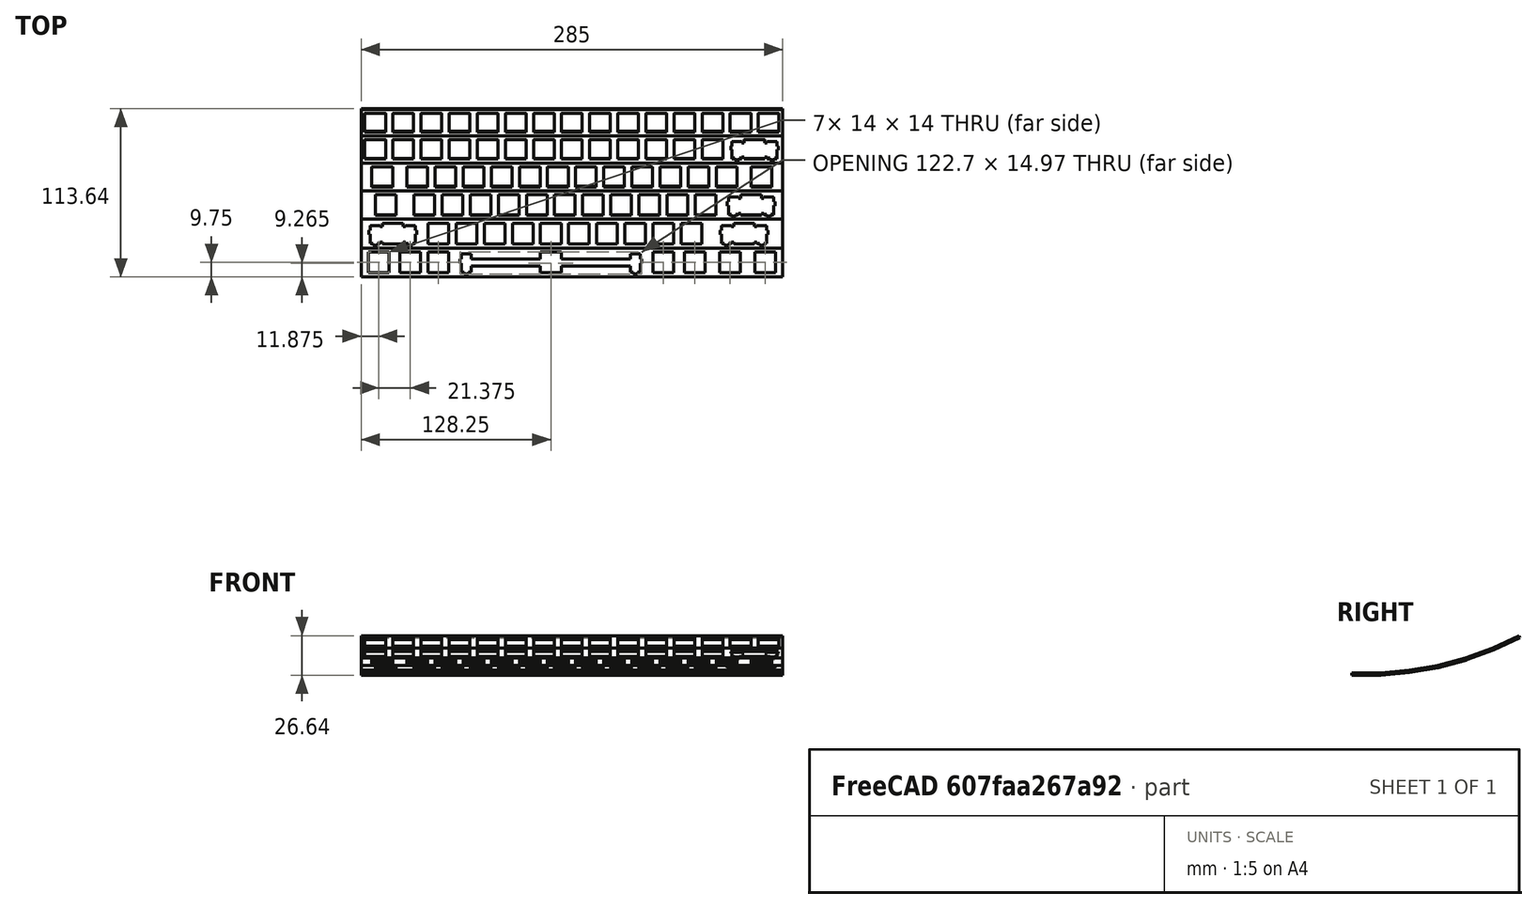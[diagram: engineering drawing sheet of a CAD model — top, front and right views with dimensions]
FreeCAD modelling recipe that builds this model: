
FCSTD DOCUMENT  (FreeCAD 1.0R38641 +468 (Git))
Label: case
License: GPL 3
objects: Sketcher::SketchObject×16, PartDesign::Pocket×15, PartDesign::LinearPattern×13, App::Part×2, Spreadsheet::Sheet×1, PartDesign::Pad×1, PartDesign::Body×1, App::FeaturePython×1, Assembly::JointGroup×1, Assembly::AssemblyObject×1
note: 107 computed .brp shape members not serialized (recipe doc carries the construction recipe); baked Part::Feature solids carry a one-line shape summary decoded from their .brp

FEATURE [Spreadsheet::Sheet] Spreadsheet  label="params"
  cells = A1='Parameter Name; B1='Value; C1='Note; A2='plate_thickness; B2(plate_thickness)==1.6 mm; A3='spacing_x; B3(spacing_x)==19 mm; A4='spacing_y; B4(spacing_y)==19.5 mm; A5='switch_width; B5(switch_width)==14 mm; A6='row_angle; B6(row_angle)==5 deg; A7='row_count; B7(row_count)=6; A8='column_count; B8(column_count)=15; A9='ctrlKey_width; B9(ctrlKey_width)=1.25; A10='enterKey_width; B10(enterKey_width)=2.25; A11='shiftKey_width; B11(shiftKey_width)=2.75; C11='Right Shift; A12='capsKey_width; B12(capsKey_width)=1.75; A13='tabKey_width; B13(tabKey_width)=1.5; A14='spaceBar_width; B14(spaceBar_width)=7; A15='backspace_width; B15(backspace_width)=2
FEATURE [Sketcher::SketchObject] Sketch  label="Profile"
  ArcFitTolerance = 1e-06
  FullyConstrained = true
  MakeInternals = false
  Placement = pos=(0,0,0) rot=(0.57735,0.57735,0.57735;2.0944rad)
  expr: Constraints[10] = <<params>>.spacing_y
  expr: Constraints[20] = <<params>>.row_angle
  expr: Constraints[52] = <<params>>.row_angle
  expr: Constraints[61] = <<params>>.row_angle
  expr: Constraints[62] = <<params>>.row_angle
  expr: Constraints[63] = <<params>>.row_angle
  expr: Constraints[9] = <<params>>.plate_thickness
  sketch-geometry (29):
    g0: LineSegment StartX=0 StartY=0 StartZ=0 EndX=19.5 EndY=0 EndZ=0
    g1: LineSegment [constr] StartX=19.5 StartY=0 StartZ=0 EndX=19.5 EndY=1.6 EndZ=0
    g2: LineSegment StartX=19.5 StartY=1.6 StartZ=0 EndX=0 EndY=1.6 EndZ=0
    g3: LineSegment StartX=0 StartY=1.6 StartZ=0 EndX=0 EndY=0 EndZ=0
    g4: LineSegment [constr] StartX=19.5 StartY=1.6 StartZ=0 EndX=19.6394 EndY=0.00608848 EndZ=0
    g5: LineSegment StartX=19.6394 StartY=0.00608848 StartZ=0 EndX=39.0652 EndY=1.70563 EndZ=0
    g6: LineSegment [constr] StartX=39.0652 StartY=1.70563 StartZ=0 EndX=38.9258 EndY=3.29954 EndZ=0
    g7: LineSegment StartX=38.9258 StartY=3.29954 StartZ=0 EndX=19.5 EndY=1.6 EndZ=0
    g8: LineSegment [constr] StartX=38.9258 StartY=3.29954 StartZ=0 EndX=39.2036 EndY=1.72384 EndZ=0
    g9: LineSegment StartX=39.2036 StartY=1.72384 StartZ=0 EndX=58.4074 EndY=5.10998 EndZ=0
    g10: LineSegment [constr] StartX=58.4074 StartY=5.10998 StartZ=0 EndX=58.1295 EndY=6.68568 EndZ=0
    g11: LineSegment StartX=58.1295 StartY=6.68568 StartZ=0 EndX=38.9258 EndY=3.29954 EndZ=0
    g12: LineSegment [constr] StartX=58.1295 StartY=6.68568 StartZ=0 EndX=58.5437 EndY=5.1402 EndZ=0
    g13: LineSegment StartX=58.5437 StartY=5.1402 StartZ=0 EndX=77.3792 EndY=10.1872 EndZ=0
    g14: LineSegment [constr] StartX=77.3792 StartY=10.1872 StartZ=0 EndX=76.9651 EndY=11.7326 EndZ=0
    g15: LineSegment StartX=76.9651 StartY=11.7326 StartZ=0 EndX=58.1295 EndY=6.68568 EndZ=0
    g16: LineSegment [constr] StartX=76.9651 StartY=11.7326 StartZ=0 EndX=77.5123 EndY=10.2291 EndZ=0
    g17: LineSegment StartX=77.5123 StartY=10.2291 StartZ=0 EndX=95.8363 EndY=16.8985 EndZ=0
    g18: LineSegment [constr] StartX=95.8363 StartY=16.8985 StartZ=0 EndX=95.2891 EndY=18.402 EndZ=0
    g19: LineSegment StartX=95.2891 StartY=18.402 StartZ=0 EndX=76.9651 EndY=11.7326 EndZ=0
    g20: LineSegment [constr] StartX=95.2891 StartY=18.402 StartZ=0 EndX=95.9653 EndY=16.9519 EndZ=0
    g21: LineSegment StartX=95.9653 StartY=16.9519 StartZ=0 EndX=113.638 EndY=25.193 EndZ=0
    g22: LineSegment StartX=113.638 StartY=25.193 StartZ=0 EndX=112.962 EndY=26.6431 EndZ=0
    g23: LineSegment StartX=112.962 StartY=26.6431 StartZ=0 EndX=95.2891 EndY=18.402 EndZ=0
    g24: ArcOfCircle CenterX=19.5 CenterY=1.6 CenterZ=0 NormalX=0 NormalY=0 NormalZ=1 AngleXU=0 Radius=1.6 StartAngle=4.71239 EndAngle=4.79966
    g25: ArcOfCircle CenterX=38.9258 CenterY=3.29954 CenterZ=0 NormalX=0 NormalY=0 NormalZ=1 AngleXU=0 Radius=1.6 StartAngle=4.79966 EndAngle=4.88692
    g26: ArcOfCircle CenterX=58.1295 CenterY=6.68568 CenterZ=0 NormalX=0 NormalY=0 NormalZ=1 AngleXU=0 Radius=1.6 StartAngle=4.88692 EndAngle=4.97419
    g27: ArcOfCircle CenterX=76.9651 CenterY=11.7326 CenterZ=0 NormalX=0 NormalY=0 NormalZ=1 AngleXU=0 Radius=1.6 StartAngle=4.97419 EndAngle=5.06145
    g28: ArcOfCircle CenterX=95.2891 CenterY=18.402 CenterZ=0 NormalX=0 NormalY=0 NormalZ=1 AngleXU=0 Radius=1.6 StartAngle=5.06145 EndAngle=5.14872
  constraints (76):
    c: Coincident(g0,g1)
    c: Coincident(g1,g2)
    c: Coincident(g2,g3)
    c: Coincident(g3,g0)
    c: Horizontal(g0)
    c: Horizontal(g2)
    c: Vertical(g1)
    c: Vertical(g3)
    c: Coincident(g0,g-1)
    c: DistanceY(g3,g3) = 1.6
    c: DistanceX(g2,g2) = 19.5
    c: Coincident(g4,g5)
    c: Coincident(g5,g6)
    c: Coincident(g6,g7)
    c: Coincident(g7,g4)
    c: Perpendicular(g7,g4)
    c: Perpendicular(g6,g7)
    c: Perpendicular(g5,g4)
    c: Equal(g7,g2)
    c: Coincident(g4,g1)
    c: Angle(g2,g7) = 0.0872665
    c: Coincident(g8,g9)
    c: Coincident(g9,g10)
    c: Coincident(g11,g8)
    c: Perpendicular(g11,g8)
    c: Perpendicular(g10,g11)
    c: Perpendicular(g9,g8)
    c: Coincident(g12,g13)
    c: Coincident(g13,g14)
    c: Coincident(g14,g15)
    c: Perpendicular(g15,g12)
    c: Perpendicular(g14,g15)
    c: Perpendicular(g13,g12)
    c: Coincident(g16,g17)
    c: Coincident(g17,g18)
    c: Coincident(g18,g19)
    c: Coincident(g19,g16)
    c: Perpendicular(g19,g16)
    c: Perpendicular(g18,g19)
    c: Perpendicular(g17,g16)
    c: Coincident(g20,g21)
    c: Coincident(g21,g22)
    c: Coincident(g22,g23)
    c: Coincident(g23,g20)
    c: Perpendicular(g23,g20)
    c: Perpendicular(g22,g23)
    c: Perpendicular(g21,g20)
    c: Equal(g11,g15)
    c: Equal(g15,g19)
    c: Equal(g19,g23)
    c: Equal(g23,g7)
    c: Coincident(g6,g8)
    c: Angle(g11,g15) = 0.0872665
    c: Coincident(g14,g16)
    c: Coincident(g20,g18)
    c: Coincident(g26,g9)
    c: Coincident(g26,g12)
    c: Coincident(g28,g18)
    c: Coincident(g28,g17)
    c: Coincident(g28,g20)
    c: Coincident(g25,g8)
    c: Angle(g7,g11) = 0.0872665
    c: Angle(g15,g19) = 0.0872665
    c: Angle(g19,g23) = 0.0872665
    c: Coincident(g25,g6)
    c: Coincident(g24,g0)
    c: Coincident(g24,g1)
    c: Coincident(g24,g4)
    c: Coincident(g25,g5)
    c: Coincident(g27,g13)
    c: Coincident(g27,g16)
    c: Coincident(g27,g14)
    c: Coincident(g26,g15)
    c: Coincident(g26,g12)
    c: Coincident(g26,g10)
    c: Coincident(g26,g11)
FEATURE [PartDesign::Pad] Pad
  Direction = (1,1e-16,-1e-16)
  Length = 285
  Length2 = 10
  Placement = pos=(0,0,0) rot=(0.57735,0.57735,0.57735;2.0944rad)
  Profile = -> Sketch
  ReferenceAxis = -> Sketch [N_Axis]
  Refine = true
  Suppressed = false
  Type = 0
  expr: Length = <<params>>.column_count * <<params>>.spacing_x
FEATURE [Sketcher::SketchObject] Sketch001
  ArcFitTolerance = 1e-06
  AttachmentSupport = -> [Pad]
  FullyConstrained = true
  MakeInternals = false
  MapMode = 5
  Placement = pos=(4e-16,-7e-16,1.6) rot=(0,0,-1;1.5708rad)
  expr: Constraints[11] = <<params>>.spacing_y / 2
  expr: Constraints[12] = (<<params>>.ctrlKey_width + 0.5) * <<params>>.spacing_x
  expr: Constraints[9] = <<params>>.switch_width
  sketch-geometry (5):
    g0: LineSegment StartX=-16.75 StartY=26.25 StartZ=0 EndX=-2.75 EndY=26.25 EndZ=0
    g1: LineSegment StartX=-2.75 StartY=26.25 StartZ=0 EndX=-2.75 EndY=40.25 EndZ=0
    g2: LineSegment StartX=-2.75 StartY=40.25 StartZ=0 EndX=-16.75 EndY=40.25 EndZ=0
    g3: LineSegment StartX=-16.75 StartY=40.25 StartZ=0 EndX=-16.75 EndY=26.25 EndZ=0
    g4: GeomPoint [constr] X=-9.75 Y=33.25 Z=0
  constraints (13):
    c: Coincident(g0,g1)
    c: Coincident(g1,g2)
    c: Coincident(g2,g3)
    c: Coincident(g3,g0)
    c: Horizontal(g0)
    c: Horizontal(g2)
    c: Vertical(g1)
    c: Vertical(g3)
    c: Symmetric(g2,g0,g4)
    c: DistanceX(g0,g0) = 14
    c: Equal(g0,g3)
    c: Distance(g4,g-2) = 9.75
    c: Distance(g4,g-1) = 33.25
FEATURE [Sketcher::SketchObject] Sketch002
  ArcFitTolerance = 1e-06
  AttachmentSupport = -> [Pad]
  ExternalGeometry = -> [Pad]
  FullyConstrained = true
  MakeInternals = false
  MapMode = 5
  Placement = pos=(0,0.00920587,-0.105224) rot=(0.043578,0.043578,-0.998099;1.5727rad)
  expr: Constraints[11] = (<<params>>.enterKey_width + 0.5) * <<params>>.spacing_x
  expr: Constraints[12] = <<params>>.spacing_y / 2
  expr: Constraints[9] = <<params>>.switch_width
  sketch-geometry (5):
    g0: LineSegment StartX=-36.3152 StartY=45.25 StartZ=0 EndX=-22.3152 EndY=45.25 EndZ=0
    g1: LineSegment StartX=-22.3152 StartY=45.25 StartZ=0 EndX=-22.3152 EndY=59.25 EndZ=0
    g2: LineSegment StartX=-22.3152 StartY=59.25 StartZ=0 EndX=-36.3152 EndY=59.25 EndZ=0
    g3: LineSegment StartX=-36.3152 StartY=59.25 StartZ=0 EndX=-36.3152 EndY=45.25 EndZ=0
    g4: GeomPoint [constr] X=-29.3152 Y=52.25 Z=0
  constraints (13):
    c: Coincident(g0,g1)
    c: Coincident(g1,g2)
    c: Coincident(g2,g3)
    c: Coincident(g3,g0)
    c: Horizontal(g0)
    c: Horizontal(g2)
    c: Vertical(g1)
    c: Vertical(g3)
    c: Symmetric(g2,g0,g4)
    c: DistanceX(g0,g0) = 14
    c: Equal(g0,g3)
    c: Distance(g4,g-1) = 52.25
    c: Distance(g4,g-3) = 9.75
FEATURE [Sketcher::SketchObject] Sketch003
  ArcFitTolerance = 1e-06
  AttachmentSupport = -> [Pad]
  ExternalGeometry = -> [Pad]
  FullyConstrained = true
  MakeInternals = false
  MapMode = 5
  Placement = pos=(-1.1e-15,0.609502,-3.45666) rot=(0.086827,0.086827,-0.992433;1.57839rad)
  expr: Constraints[11] = (<<params>>.capsKey_width + 0.5) * <<params>>.spacing_x
  expr: Constraints[12] = <<params>>.spacing_y / 2
  expr: Constraints[9] = <<params>>.switch_width
  sketch-geometry (5):
    g0: LineSegment StartX=-55.6574 StartY=35.75 StartZ=0 EndX=-41.6574 EndY=35.75 EndZ=0
    g1: LineSegment StartX=-41.6574 StartY=35.75 StartZ=0 EndX=-41.6574 EndY=49.75 EndZ=0
    g2: LineSegment StartX=-41.6574 StartY=49.75 StartZ=0 EndX=-55.6574 EndY=49.75 EndZ=0
    g3: LineSegment StartX=-55.6574 StartY=49.75 StartZ=0 EndX=-55.6574 EndY=35.75 EndZ=0
    g4: GeomPoint [constr] X=-48.6574 Y=42.75 Z=0
  constraints (13):
    c: Coincident(g0,g1)
    c: Coincident(g1,g2)
    c: Coincident(g2,g3)
    c: Coincident(g3,g0)
    c: Horizontal(g0)
    c: Horizontal(g2)
    c: Vertical(g1)
    c: Vertical(g3)
    c: Symmetric(g2,g0,g4)
    c: DistanceX(g0,g0) = 14
    c: Equal(g0,g3)
    c: Distance(g4,g-1) = 42.75
    c: Distance(g4,g-3) = 9.75
FEATURE [Sketcher::SketchObject] Sketch004
  ArcFitTolerance = 1e-06
  AttachmentSupport = -> [Pad]
  ExternalGeometry = -> [Pad]
  FullyConstrained = true
  MakeInternals = false
  MapMode = 5
  Placement = pos=(-3.1e-15,2.22252,-8.29457) rot=(0.129428,0.129428,-0.983106;1.58783rad)
  expr: Constraints[11] = (<<params>>.tabKey_width + 0.5) * <<params>>.spacing_x
  expr: Constraints[12] = <<params>>.spacing_y / 2
  expr: Constraints[9] = <<params>>.switch_width
  sketch-geometry (5):
    g0: LineSegment StartX=-74.6292 StartY=31 StartZ=0 EndX=-60.6292 EndY=31 EndZ=0
    g1: LineSegment StartX=-60.6292 StartY=31 StartZ=0 EndX=-60.6292 EndY=45 EndZ=0
    g2: LineSegment StartX=-60.6292 StartY=45 StartZ=0 EndX=-74.6292 EndY=45 EndZ=0
    g3: LineSegment StartX=-74.6292 StartY=45 StartZ=0 EndX=-74.6292 EndY=31 EndZ=0
    g4: GeomPoint [constr] X=-67.6292 Y=38 Z=0
  constraints (13):
    c: Coincident(g0,g1)
    c: Coincident(g1,g2)
    c: Coincident(g2,g3)
    c: Coincident(g3,g0)
    c: Horizontal(g0)
    c: Horizontal(g2)
    c: Vertical(g1)
    c: Vertical(g3)
    c: Symmetric(g2,g0,g4)
    c: DistanceX(g0,g0) = 14
    c: Equal(g0,g3)
    c: Distance(g4,g-1) = 38
    c: Distance(g4,g-3) = 9.75
FEATURE [Sketcher::SketchObject] Sketch005
  ArcFitTolerance = 1e-06
  AttachmentSupport = -> [Pad]
  ExternalGeometry = -> [Pad]
  FullyConstrained = true
  MakeInternals = false
  MapMode = 5
  Placement = pos=(-6.1e-15,5.23241,-14.3759) rot=(0.171088,0.171088,-0.970288;1.60095rad)
  expr: Constraints[11] = 0.5 * <<params>>.spacing_x
  expr: Constraints[12] = <<params>>.spacing_y / 2
  expr: Constraints[9] = <<params>>.switch_width
  sketch-geometry (5):
    g0: LineSegment StartX=-93.0863 StartY=2.5 StartZ=0 EndX=-79.0863 EndY=2.5 EndZ=0
    g1: LineSegment StartX=-79.0863 StartY=2.5 StartZ=0 EndX=-79.0863 EndY=16.5 EndZ=0
    g2: LineSegment StartX=-79.0863 StartY=16.5 StartZ=0 EndX=-93.0863 EndY=16.5 EndZ=0
    g3: LineSegment StartX=-93.0863 StartY=16.5 StartZ=0 EndX=-93.0863 EndY=2.5 EndZ=0
    g4: GeomPoint [constr] X=-86.0863 Y=9.5 Z=0
  constraints (13):
    c: Coincident(g0,g1)
    c: Coincident(g1,g2)
    c: Coincident(g2,g3)
    c: Coincident(g3,g0)
    c: Horizontal(g0)
    c: Horizontal(g2)
    c: Vertical(g1)
    c: Vertical(g3)
    c: Symmetric(g2,g0,g4)
    c: DistanceX(g0,g0) = 14
    c: Equal(g0,g3)
    c: Distance(g4,g-1) = 9.5
    c: Distance(g4,g-3) = 9.75
FEATURE [Sketcher::SketchObject] Sketch006
  ArcFitTolerance = 1e-06
  AttachmentSupport = -> [Pad]
  ExternalGeometry = -> [Pad]
  FullyConstrained = true
  MakeInternals = false
  MapMode = 5
  Placement = pos=(-1.03e-14,9.97083,-21.3825) rot=(0.211541,0.211541,-0.954201;1.61766rad)
  expr: Constraints[11] = 0.5 * <<params>>.spacing_x
  expr: Constraints[12] = <<params>>.spacing_y / 2
  expr: Constraints[9] = <<params>>.switch_width
  sketch-geometry (5):
    g0: LineSegment StartX=-110.888 StartY=2.5 StartZ=0 EndX=-96.8883 EndY=2.5 EndZ=0
    g1: LineSegment StartX=-96.8883 StartY=2.5 StartZ=0 EndX=-96.8883 EndY=16.5 EndZ=0
    g2: LineSegment StartX=-96.8883 StartY=16.5 StartZ=0 EndX=-110.888 EndY=16.5 EndZ=0
    g3: LineSegment StartX=-110.888 StartY=16.5 StartZ=0 EndX=-110.888 EndY=2.5 EndZ=0
    g4: GeomPoint [constr] X=-103.888 Y=9.5 Z=0
  constraints (13):
    c: Coincident(g0,g1)
    c: Coincident(g1,g2)
    c: Coincident(g2,g3)
    c: Coincident(g3,g0)
    c: Horizontal(g0)
    c: Horizontal(g2)
    c: Vertical(g1)
    c: Vertical(g3)
    c: Symmetric(g2,g0,g4)
    c: DistanceX(g0,g0) = 14
    c: Equal(g0,g3)
    c: Distance(g4,g-1) = 9.5
    c: Distance(g4,g-3) = 9.75
FEATURE [PartDesign::Pocket] Pocket
  BaseFeature = -> Pad
  Direction = (0,0,-1)
  Length = 5
  Length2 = 5
  Placement = pos=(0,0,0) rot=(0.57735,0.57735,0.57735;2.0944rad)
  Profile = -> Sketch001
  ReferenceAxis = -> Sketch001 [N_Axis]
  Refine = true
  Suppressed = false
  Type = 2
FEATURE [PartDesign::Pocket] Pocket001
  BaseFeature = -> Pocket
  Direction = (0,0.0871557,-0.996195)
  Length = 5
  Length2 = 5
  Placement = pos=(0,0,0) rot=(0.57735,0.57735,0.57735;2.0944rad)
  Profile = -> Sketch002
  ReferenceAxis = -> Sketch002 [N_Axis]
  Refine = true
  Suppressed = false
  Type = 2
FEATURE [PartDesign::Pocket] Pocket002
  BaseFeature = -> Pocket001
  Direction = (0,0.173648,-0.984808)
  Length = 5
  Length2 = 5
  Placement = pos=(0,0,0) rot=(0.57735,0.57735,0.57735;2.0944rad)
  Profile = -> Sketch003
  ReferenceAxis = -> Sketch003 [N_Axis]
  Refine = true
  Suppressed = false
  Type = 2
FEATURE [PartDesign::Pocket] Pocket003
  BaseFeature = -> Pocket002
  Direction = (0,0.258819,-0.965926)
  Length = 5
  Length2 = 5
  Placement = pos=(0,0,0) rot=(0.57735,0.57735,0.57735;2.0944rad)
  Profile = -> Sketch004
  ReferenceAxis = -> Sketch004 [N_Axis]
  Refine = true
  Suppressed = false
  Type = 2
FEATURE [PartDesign::Pocket] Pocket004
  BaseFeature = -> Pocket003
  Direction = (-1e-16,0.34202,-0.939693)
  Length = 5
  Length2 = 5
  Placement = pos=(0,0,0) rot=(0.57735,0.57735,0.57735;2.0944rad)
  Profile = -> Sketch005
  ReferenceAxis = -> Sketch005 [N_Axis]
  Refine = true
  Suppressed = false
  Type = 2
FEATURE [PartDesign::Pocket] Pocket005
  BaseFeature = -> Pocket004
  Direction = (-1e-16,0.422618,-0.906308)
  Length = 5
  Length2 = 5
  Placement = pos=(0,0,0) rot=(0.57735,0.57735,0.57735;2.0944rad)
  Profile = -> Sketch006
  ReferenceAxis = -> Sketch006 [N_Axis]
  Refine = true
  Suppressed = false
  Type = 2
FEATURE [PartDesign::LinearPattern] LinearPattern
  BaseFeature = -> Pocket005
  Direction = -> X_Axis002
  Length = 266
  Mode = 1
  Occurrences = 15
  Offset = 19
  Originals = -> [Pocket005]
  Placement = pos=(0,0,0) rot=(0.57735,0.57735,0.57735;2.0944rad)
  Refine = true
  Suppressed = false
  TransformMode = 0
  expr: Occurrences = <<params>>.column_count
  expr: Offset = <<params>>.spacing_x
FEATURE [PartDesign::LinearPattern] LinearPattern001
  BaseFeature = -> LinearPattern
  Direction = -> X_Axis002
  Length = 228
  Mode = 1
  Occurrences = 13
  Offset = 19
  Originals = -> [Pocket004]
  Placement = pos=(0,0,0) rot=(0.57735,0.57735,0.57735;2.0944rad)
  Refine = true
  Suppressed = false
  TransformMode = 0
  expr: Occurrences = <<params>>.column_count - <<params>>.backspace_width
  expr: Offset = <<params>>.spacing_x
FEATURE [PartDesign::LinearPattern] LinearPattern002
  BaseFeature = -> LinearPattern001
  Direction = -> X_Axis002
  Length = 19
  Mode = 1
  Occurrences = 2
  Offset = 19
  Originals = -> [Pocket]
  Placement = pos=(0,0,0) rot=(0.57735,0.57735,0.57735;2.0944rad)
  Refine = true
  Suppressed = false
  TransformMode = 0
  expr: Offset = <<params>>.spacing_x
FEATURE [PartDesign::LinearPattern] LinearPattern003
  BaseFeature = -> LinearPattern002
  Direction = -> X_Axis002
  Length = 171
  Mode = 1
  Occurrences = 10
  Offset = 19
  Originals = -> [Pocket001]
  Placement = pos=(0,0,0) rot=(0.57735,0.57735,0.57735;2.0944rad)
  Refine = true
  Suppressed = false
  TransformMode = 0
  expr: Occurrences = <<params>>.column_count - <<params>>.enterKey_width - <<params>>.shiftKey_width
  expr: Offset = <<params>>.spacing_x
FEATURE [PartDesign::LinearPattern] LinearPattern004
  BaseFeature = -> LinearPattern003
  Direction = -> X_Axis002
  Length = 190
  Mode = 1
  Occurrences = 11
  Offset = 19
  Originals = -> [Pocket002]
  Placement = pos=(0,0,0) rot=(0.57735,0.57735,0.57735;2.0944rad)
  Refine = true
  Suppressed = false
  TransformMode = 0
  expr: Occurrences = <<params>>.column_count - <<params>>.capsKey_width - <<params>>.enterKey_width
  expr: Offset = <<params>>.spacing_x
FEATURE [PartDesign::LinearPattern] LinearPattern005
  BaseFeature = -> LinearPattern004
  Direction = -> X_Axis002
  Length = 209
  Mode = 1
  Occurrences = 12
  Offset = 19
  Originals = -> [Pocket003]
  Placement = pos=(0,0,0) rot=(0.57735,0.57735,0.57735;2.0944rad)
  Refine = true
  Suppressed = false
  TransformMode = 0
  expr: Occurrences = <<params>>.column_count - 2 * <<params>>.tabKey_width
  expr: Offset = <<params>>.spacing_x
FEATURE [PartDesign::LinearPattern] LinearPattern006
  BaseFeature = -> LinearPattern005
  Direction = -> X_Axis002
  Length = 21.375
  Mode = 1
  Occurrences = 2
  Offset = 21.375
  Originals = -> [Pocket]
  Placement = pos=(0,0,0) rot=(0.57735,0.57735,0.57735;2.0944rad)
  Refine = true
  Reversed = true
  Suppressed = false
  TransformMode = 0
  expr: Offset = <<params>>.spacing_x * (<<params>>.ctrlKey_width + 1) / 2
FEATURE [PartDesign::LinearPattern] LinearPattern007
  BaseFeature = -> LinearPattern006
  Direction = -> X_Axis002
  Length = 30.875
  Mode = 1
  Occurrences = 2
  Offset = 30.875
  Originals = -> [Pocket001]
  Placement = pos=(0,0,0) rot=(0.57735,0.57735,0.57735;2.0944rad)
  Refine = true
  Reversed = true
  Suppressed = false
  TransformMode = 0
  expr: Offset = (<<params>>.enterKey_width + 1) * <<params>>.spacing_x / 2
FEATURE [PartDesign::LinearPattern] LinearPattern008
  BaseFeature = -> LinearPattern007
  Direction = -> X_Axis002
  Length = 26.125
  Mode = 1
  Occurrences = 2
  Offset = 26.125
  Originals = -> [Pocket002]
  Placement = pos=(0,0,0) rot=(0.57735,0.57735,0.57735;2.0944rad)
  Refine = true
  Reversed = true
  Suppressed = false
  TransformMode = 0
  expr: Offset = (<<params>>.capsKey_width + 1) * <<params>>.spacing_x / 2
FEATURE [PartDesign::LinearPattern] LinearPattern009
  BaseFeature = -> LinearPattern008
  Direction = -> X_Axis002
  Length = 23.75
  Mode = 1
  Occurrences = 2
  Offset = 23.75
  Originals = -> [Pocket003]
  Placement = pos=(0,0,0) rot=(0.57735,0.57735,0.57735;2.0944rad)
  Refine = true
  Reversed = true
  Suppressed = false
  TransformMode = 0
  expr: Offset = (<<params>>.tabKey_width + 1) * <<params>>.spacing_x / 2
FEATURE [Sketcher::SketchObject] Sketch007
  ArcFitTolerance = 1e-06
  AttachmentSupport = -> [Pad]
  FullyConstrained = true
  MakeInternals = false
  MapMode = 5
  Placement = pos=(4e-16,-7e-16,1.6) rot=(0,0,-1;1.5708rad)
  expr: Constraints[11] = <<params>>.spacing_y / 2
  expr: Constraints[12] = <<params>>.spacing_x * (<<params>>.ctrlKey_width + 2 + <<params>>.spaceBar_width / 2)
  expr: Constraints[33] = 114.3 + 6.65
  expr: Constraints[95] = 4.2 - 6.65 / 2
  expr: Constraints[9] = <<params>>.switch_width
  sketch-geometry (35):
    g0: LineSegment StartX=-16.75 StartY=121.25 StartZ=0 EndX=-2.75 EndY=121.25 EndZ=0
    g1: LineSegment StartX=-2.75 StartY=121.25 StartZ=0 EndX=-2.75 EndY=135.25 EndZ=0
    g2: LineSegment StartX=-2.75 StartY=135.25 StartZ=0 EndX=-16.75 EndY=135.25 EndZ=0
    g3: LineSegment StartX=-16.75 StartY=135.25 StartZ=0 EndX=-16.75 EndY=121.25 EndZ=0
    g4: GeomPoint [constr] X=-9.75 Y=128.25 Z=0
    g5: LineSegment StartX=-15.45 StartY=67.775 StartZ=0 EndX=-3.15 EndY=67.775 EndZ=0
    g6: LineSegment StartX=-3.15 StartY=67.775 StartZ=0 EndX=-3.15 EndY=74.425 EndZ=0
    g7: LineSegment StartX=-3.15 StartY=74.425 StartZ=0 EndX=-15.45 EndY=74.425 EndZ=0
    g8: LineSegment StartX=-15.45 StartY=74.425 StartZ=0 EndX=-15.45 EndY=67.775 EndZ=0
    g9: LineSegment StartX=-15.45 StartY=182.075 StartZ=0 EndX=-3.15 EndY=182.075 EndZ=0
    g10: LineSegment StartX=-3.15 StartY=182.075 StartZ=0 EndX=-3.15 EndY=188.725 EndZ=0
    g11: LineSegment StartX=-3.15 StartY=188.725 StartZ=0 EndX=-15.45 EndY=188.725 EndZ=0
    g12: LineSegment StartX=-15.45 StartY=188.725 StartZ=0 EndX=-15.45 EndY=182.075 EndZ=0
    g13: LineSegment [constr] StartX=-16.75 StartY=128.25 StartZ=0 EndX=-2.75 EndY=128.25 EndZ=0
    g14: LineSegment StartX=-12.05 StartY=67.775 StartZ=0 EndX=-12.05 EndY=66.9 EndZ=0
    g15: LineSegment StartX=-12.05 StartY=66.9 StartZ=0 EndX=-9.25 EndY=66.9 EndZ=0
    g16: LineSegment StartX=-9.25 StartY=66.9 StartZ=0 EndX=-9.25 EndY=67.775 EndZ=0
    g17: LineSegment StartX=-9.25 StartY=67.775 StartZ=0 EndX=-12.05 EndY=67.775 EndZ=0
    g18: LineSegment StartX=-3.15 StartY=69.6 StartZ=0 EndX=-1.78 EndY=69.6 EndZ=0
    g19: LineSegment StartX=-1.78 StartY=69.6 StartZ=0 EndX=-1.78 EndY=72.6 EndZ=0
    g20: LineSegment StartX=-1.78 StartY=72.6 StartZ=0 EndX=-3.15 EndY=72.6 EndZ=0
    g21: LineSegment StartX=-3.15 StartY=72.6 StartZ=0 EndX=-3.15 EndY=69.6 EndZ=0
    g22: LineSegment StartX=-9.25 StartY=188.725 StartZ=0 EndX=-9.25 EndY=189.6 EndZ=0
    g23: LineSegment StartX=-9.25 StartY=189.6 StartZ=0 EndX=-12.05 EndY=189.6 EndZ=0
    g24: LineSegment StartX=-12.05 StartY=189.6 StartZ=0 EndX=-12.05 EndY=188.725 EndZ=0
    g25: LineSegment StartX=-12.05 StartY=188.725 StartZ=0 EndX=-9.25 EndY=188.725 EndZ=0
    g26: LineSegment StartX=-3.15 StartY=183.9 StartZ=0 EndX=-1.78 EndY=183.9 EndZ=0
    g27: LineSegment StartX=-1.78 StartY=183.9 StartZ=0 EndX=-1.78 EndY=186.9 EndZ=0
    g28: LineSegment StartX=-1.78 StartY=186.9 StartZ=0 EndX=-3.15 EndY=186.9 EndZ=0
    g29: LineSegment StartX=-3.15 StartY=186.9 StartZ=0 EndX=-3.15 EndY=183.9 EndZ=0
    g30: LineSegment StartX=-7.45 StartY=182.075 StartZ=0 EndX=-12.05 EndY=182.075 EndZ=0
    g31: LineSegment StartX=-12.05 StartY=182.075 StartZ=0 EndX=-12.05 EndY=74.425 EndZ=0
    g32: LineSegment StartX=-12.05 StartY=74.425 StartZ=0 EndX=-7.45 EndY=74.425 EndZ=0
    g33: LineSegment StartX=-7.45 StartY=74.425 StartZ=0 EndX=-7.45 EndY=182.075 EndZ=0
    g34: LineSegment [constr] StartX=-9.75 StartY=128.25 StartZ=0 EndX=-9.75 EndY=74.425 EndZ=0
  constraints (98):
    c: Coincident(g0,g1)
    c: Coincident(g1,g2)
    c: Coincident(g2,g3)
    c: Coincident(g3,g0)
    c: Horizontal(g0)
    c: Horizontal(g2)
    c: Vertical(g1)
    c: Vertical(g3)
    c: Symmetric(g2,g0,g4)
    c: DistanceX(g0,g0) = 14
    c: Equal(g0,g3)
    c: Distance(g4,g-2) = 9.75
    c: DistanceY(g-1,g4) = 128.25
    c: Coincident(g5,g6)
    c: Coincident(g6,g7)
    c: Coincident(g7,g8)
    c: Coincident(g8,g5)
    c: Horizontal(g5)
    c: Horizontal(g7)
    c: Vertical(g6)
    c: Vertical(g8)
    c: Coincident(g9,g10)
    c: Coincident(g10,g11)
    c: Coincident(g11,g12)
    c: Coincident(g12,g9)
    c: Horizontal(g9)
    c: Horizontal(g11)
    c: Vertical(g10)
    c: Vertical(g12)
    c: Symmetric(g3,g3,g13)
    c: Symmetric(g1,g1,g13)
    c: DistanceX(g5,g5) = 12.3
    c: DistanceY(g8,g8) = 6.65
    c: Distance(g11,g5) = 120.95
    c: Symmetric(g7,g9,g13)
    c: Symmetric(g10,g5,g13)
    c: Coincident(g14,g15)
    c: Coincident(g15,g16)
    c: Coincident(g16,g17)
    c: Coincident(g17,g14)
    c: Vertical(g14)
    c: Vertical(g16)
    c: Horizontal(g15)
    c: Horizontal(g17)
    c: PointOnObject(g14,g5)
    c: Coincident(g18,g19)
    c: Coincident(g19,g20)
    c: Coincident(g20,g21)
    c: Coincident(g21,g18)
    c: Horizontal(g18)
    c: Horizontal(g20)
    c: Vertical(g19)
    c: Vertical(g21)
    c: PointOnObject(g18,g6)
    c: Coincident(g22,g23)
    c: Coincident(g23,g24)
    c: Coincident(g24,g25)
    c: Coincident(g25,g22)
    c: Vertical(g22)
    c: Vertical(g24)
    c: Horizontal(g23)
    c: Horizontal(g25)
    c: PointOnObject(g22,g11)
    c: Coincident(g26,g27)
    c: Coincident(g27,g28)
    c: Coincident(g28,g29)
    c: Coincident(g29,g26)
    c: Horizontal(g26)
    c: Horizontal(g28)
    c: Vertical(g27)
    c: Vertical(g29)
    c: PointOnObject(g26,g10)
    c: Coincident(g30,g31)
    c: Coincident(g31,g32)
    c: Coincident(g32,g33)
    c: Coincident(g33,g30)
    c: Horizontal(g30)
    c: Horizontal(g32)
    c: Vertical(g31)
    c: Vertical(g33)
    c: PointOnObject(g30,g9)
    c: PointOnObject(g31,g7)
    c: Symmetric(g14,g23,g13)
    c: Symmetric(g18,g27,g13)
    c: Equal(g15,g23)
    c: Equal(g19,g27)
    c: Distance(g31,g33) = 4.6
    c: DistanceX(g15,g15) = 2.8
    c: Distance(g19,g19) = 3
    c: Coincident(g34,g4)
    c: Vertical(g34)
    c: PointOnObject(g34,g7)
    c: Distance(g34,g19) = 7.97
    c: Distance(g16,g34) = 0.5
    c: Distance(g6,g34) = 6.6
    c: DistanceY(g14,g14) = 0.875
    c: Distance(g31,g34) = 2.3
    c: Distance(g5,g18) = 1.825
FEATURE [Sketcher::SketchObject] Sketch008
  ArcFitTolerance = 1e-06
  AttachmentSupport = -> [Pad]
  ExternalGeometry = -> [Pad]
  FullyConstrained = true
  MakeInternals = false
  MapMode = 5
  Placement = pos=(4e-16,-7e-16,1.6) rot=(0,0,-1;1.5708rad)
  expr: Constraints[11] = <<params>>.spacing_y / 2
  expr: Constraints[12] = <<params>>.ctrlKey_width * <<params>>.spacing_x / 2
  expr: Constraints[9] = <<params>>.switch_width
  sketch-geometry (5):
    g0: LineSegment StartX=-16.75 StartY=266.125 StartZ=0 EndX=-2.75 EndY=266.125 EndZ=0
    g1: LineSegment StartX=-2.75 StartY=266.125 StartZ=0 EndX=-2.75 EndY=280.125 EndZ=0
    g2: LineSegment StartX=-2.75 StartY=280.125 StartZ=0 EndX=-16.75 EndY=280.125 EndZ=0
    g3: LineSegment StartX=-16.75 StartY=280.125 StartZ=0 EndX=-16.75 EndY=266.125 EndZ=0
    g4: GeomPoint [constr] X=-9.75 Y=273.125 Z=0
  constraints (13):
    c: Coincident(g0,g1)
    c: Coincident(g1,g2)
    c: Coincident(g2,g3)
    c: Coincident(g3,g0)
    c: Horizontal(g0)
    c: Horizontal(g2)
    c: Vertical(g1)
    c: Vertical(g3)
    c: Symmetric(g2,g0,g4)
    c: DistanceX(g0,g0) = 14
    c: Equal(g0,g3)
    c: Distance(g4,g-2) = 9.75
    c: Distance(g4,g-3) = 11.875
FEATURE [Sketcher::SketchObject] Sketch009
  ArcFitTolerance = 1e-06
  AttachmentSupport = -> [Pad]
  ExternalGeometry = -> [Pad]
  FullyConstrained = true
  MakeInternals = false
  MapMode = 5
  Placement = pos=(0,0.00920587,-0.105224) rot=(0.043578,0.043578,-0.998099;1.5727rad)
  expr: Constraints[11] = <<params>>.spacing_y / 2
  expr: Constraints[12] = <<params>>.spacing_x * <<params>>.shiftKey_width / 2
  expr: Constraints[9] = <<params>>.switch_width
  sketch-geometry (5):
    g0: LineSegment StartX=-36.3152 StartY=251.875 StartZ=0 EndX=-22.3152 EndY=251.875 EndZ=0
    g1: LineSegment StartX=-22.3152 StartY=251.875 StartZ=0 EndX=-22.3152 EndY=265.875 EndZ=0
    g2: LineSegment StartX=-22.3152 StartY=265.875 StartZ=0 EndX=-36.3152 EndY=265.875 EndZ=0
    g3: LineSegment StartX=-36.3152 StartY=265.875 StartZ=0 EndX=-36.3152 EndY=251.875 EndZ=0
    g4: GeomPoint [constr] X=-29.3152 Y=258.875 Z=0
  constraints (13):
    c: Coincident(g0,g1)
    c: Coincident(g1,g2)
    c: Coincident(g2,g3)
    c: Coincident(g3,g0)
    c: Horizontal(g0)
    c: Horizontal(g2)
    c: Vertical(g1)
    c: Vertical(g3)
    c: Symmetric(g2,g0,g4)
    c: DistanceX(g0,g0) = 14
    c: Equal(g0,g3)
    c: Distance(g4,g-3) = 9.75
    c: Distance(g4,g-4) = 26.125
FEATURE [Sketcher::SketchObject] Sketch010
  ArcFitTolerance = 1e-06
  AttachmentSupport = -> [Pad]
  ExternalGeometry = -> [Pad]
  FullyConstrained = true
  MakeInternals = false
  MapMode = 5
  Placement = pos=(-1.1e-15,0.609502,-3.45666) rot=(0.086827,0.086827,-0.992433;1.57839rad)
  expr: Constraints[11] = <<params>>.spacing_y / 2
  expr: Constraints[12] = <<params>>.spacing_x * <<params>>.enterKey_width / 2
  expr: Constraints[9] = <<params>>.switch_width
  sketch-geometry (5):
    g0: LineSegment StartX=-55.6574 StartY=256.625 StartZ=0 EndX=-41.6574 EndY=256.625 EndZ=0
    g1: LineSegment StartX=-41.6574 StartY=256.625 StartZ=0 EndX=-41.6574 EndY=270.625 EndZ=0
    g2: LineSegment StartX=-41.6574 StartY=270.625 StartZ=0 EndX=-55.6574 EndY=270.625 EndZ=0
    g3: LineSegment StartX=-55.6574 StartY=270.625 StartZ=0 EndX=-55.6574 EndY=256.625 EndZ=0
    g4: GeomPoint [constr] X=-48.6574 Y=263.625 Z=0
  constraints (13):
    c: Coincident(g0,g1)
    c: Coincident(g1,g2)
    c: Coincident(g2,g3)
    c: Coincident(g3,g0)
    c: Horizontal(g0)
    c: Horizontal(g2)
    c: Vertical(g1)
    c: Vertical(g3)
    c: Symmetric(g2,g0,g4)
    c: DistanceX(g0,g0) = 14
    c: Equal(g0,g3)
    c: Distance(g4,g-3) = 9.75
    c: Distance(g4,g-4) = 21.375
FEATURE [Sketcher::SketchObject] Sketch011
  ArcFitTolerance = 1e-06
  AttachmentSupport = -> [Pad]
  ExternalGeometry = -> [Pad]
  FullyConstrained = true
  MakeInternals = false
  MapMode = 5
  Placement = pos=(-3.1e-15,2.22252,-8.29457) rot=(0.129428,0.129428,-0.983106;1.58783rad)
  expr: Constraints[11] = <<params>>.spacing_y / 2
  expr: Constraints[12] = <<params>>.spacing_x * <<params>>.tabKey_width / 2
  expr: Constraints[9] = <<params>>.switch_width
  sketch-geometry (5):
    g0: LineSegment StartX=-74.6292 StartY=263.75 StartZ=0 EndX=-60.6292 EndY=263.75 EndZ=0
    g1: LineSegment StartX=-60.6292 StartY=263.75 StartZ=0 EndX=-60.6292 EndY=277.75 EndZ=0
    g2: LineSegment StartX=-60.6292 StartY=277.75 StartZ=0 EndX=-74.6292 EndY=277.75 EndZ=0
    g3: LineSegment StartX=-74.6292 StartY=277.75 StartZ=0 EndX=-74.6292 EndY=263.75 EndZ=0
    g4: GeomPoint [constr] X=-67.6292 Y=270.75 Z=0
  constraints (13):
    c: Coincident(g0,g1)
    c: Coincident(g1,g2)
    c: Coincident(g2,g3)
    c: Coincident(g3,g0)
    c: Horizontal(g0)
    c: Horizontal(g2)
    c: Vertical(g1)
    c: Vertical(g3)
    c: Symmetric(g2,g0,g4)
    c: DistanceX(g0,g0) = 14
    c: Equal(g0,g3)
    c: Distance(g4,g-3) = 9.75
    c: Distance(g4,g-4) = 14.25
FEATURE [Sketcher::SketchObject] Sketch012
  ArcFitTolerance = 1e-06
  AttachmentSupport = -> [Pad]
  ExternalGeometry = -> [Pad]
  FullyConstrained = true
  MakeInternals = false
  MapMode = 5
  Placement = pos=(-6.1e-15,5.23241,-14.3759) rot=(0.171088,0.171088,-0.970288;1.60095rad)
  expr: Constraints[11] = <<params>>.spacing_y / 2
  expr: Constraints[12] = <<params>>.spacing_x * <<params>>.backspace_width / 2
  expr: Constraints[9] = <<params>>.switch_width
  sketch-geometry (5):
    g0: LineSegment StartX=-93.0863 StartY=259 StartZ=0 EndX=-79.0863 EndY=259 EndZ=0
    g1: LineSegment StartX=-79.0863 StartY=259 StartZ=0 EndX=-79.0863 EndY=273 EndZ=0
    g2: LineSegment StartX=-79.0863 StartY=273 StartZ=0 EndX=-93.0863 EndY=273 EndZ=0
    g3: LineSegment StartX=-93.0863 StartY=273 StartZ=0 EndX=-93.0863 EndY=259 EndZ=0
    g4: GeomPoint [constr] X=-86.0863 Y=266 Z=0
  constraints (13):
    c: Coincident(g0,g1)
    c: Coincident(g1,g2)
    c: Coincident(g2,g3)
    c: Coincident(g3,g0)
    c: Horizontal(g0)
    c: Horizontal(g2)
    c: Vertical(g1)
    c: Vertical(g3)
    c: Symmetric(g2,g0,g4)
    c: DistanceX(g0,g0) = 14
    c: Equal(g0,g3)
    c: Distance(g4,g-3) = 9.75
    c: Distance(g4,g-4) = 19
FEATURE [PartDesign::LinearPattern] LinearPattern010
  BaseFeature = -> LinearPattern009
  Direction = -> X_Axis002
  Length = 171
  Mode = 1
  Occurrences = 2
  Offset = 171
  Originals = -> [Pocket]
  Placement = pos=(0,0,0) rot=(0.57735,0.57735,0.57735;2.0944rad)
  Refine = true
  Suppressed = false
  TransformMode = 0
  expr: Offset = <<params>>.spacing_x * (2 + <<params>>.spaceBar_width)
FEATURE [PartDesign::Pocket] Pocket006
  BaseFeature = -> LinearPattern010
  Direction = (0,0,-1)
  Length = 5
  Length2 = 5
  Placement = pos=(0,0,0) rot=(0.57735,0.57735,0.57735;2.0944rad)
  Profile = -> Sketch007
  ReferenceAxis = -> Sketch007 [N_Axis]
  Refine = true
  Suppressed = false
  Type = 2
FEATURE [PartDesign::Pocket] Pocket007
  BaseFeature = -> Pocket006
  Direction = (0,0,-1)
  Length = 5
  Length2 = 5
  Placement = pos=(0,0,0) rot=(0.57735,0.57735,0.57735;2.0944rad)
  Profile = -> Sketch008
  ReferenceAxis = -> Sketch008 [N_Axis]
  Refine = true
  Suppressed = false
  Type = 2
FEATURE [PartDesign::Pocket] Pocket008
  BaseFeature = -> Pocket007
  Direction = (0,0.0871557,-0.996195)
  Length = 5
  Length2 = 5
  Placement = pos=(0,0,0) rot=(0.57735,0.57735,0.57735;2.0944rad)
  Profile = -> Sketch009
  ReferenceAxis = -> Sketch009 [N_Axis]
  Refine = true
  Suppressed = false
  Type = 2
FEATURE [PartDesign::Pocket] Pocket009
  BaseFeature = -> Pocket008
  Direction = (0,0.173648,-0.984808)
  Length = 5
  Length2 = 5
  Placement = pos=(0,0,0) rot=(0.57735,0.57735,0.57735;2.0944rad)
  Profile = -> Sketch010
  ReferenceAxis = -> Sketch010 [N_Axis]
  Refine = true
  Suppressed = false
  Type = 2
FEATURE [PartDesign::Pocket] Pocket010
  BaseFeature = -> Pocket009
  Direction = (0,0.258819,-0.965926)
  Length = 5
  Length2 = 5
  Placement = pos=(0,0,0) rot=(0.57735,0.57735,0.57735;2.0944rad)
  Profile = -> Sketch011
  ReferenceAxis = -> Sketch011 [N_Axis]
  Refine = true
  Suppressed = false
  Type = 2
FEATURE [PartDesign::Pocket] Pocket011
  BaseFeature = -> Pocket010
  Direction = (-1e-16,0.34202,-0.939693)
  Length = 5
  Length2 = 5
  Placement = pos=(0,0,0) rot=(0.57735,0.57735,0.57735;2.0944rad)
  Profile = -> Sketch012
  ReferenceAxis = -> Sketch012 [N_Axis]
  Refine = true
  Suppressed = false
  Type = 2
FEATURE [PartDesign::LinearPattern] LinearPattern011
  BaseFeature = -> Pocket011
  Direction = -> X_Axis002
  Length = 47.5
  Mode = 1
  Occurrences = 3
  Offset = 23.75
  Originals = -> [Pocket007]
  Placement = pos=(0,0,0) rot=(0.57735,0.57735,0.57735;2.0944rad)
  Refine = true
  Reversed = true
  Suppressed = false
  TransformMode = 0
  expr: Offset = <<params>>.spacing_x * <<params>>.ctrlKey_width
FEATURE [Sketcher::SketchObject] Sketch013
  ArcFitTolerance = 1e-06
  AttachmentSupport = -> [LinearPattern011]
  ExternalGeometry = -> [LinearPattern011]
  FullyConstrained = true
  MakeInternals = false
  MapMode = 5
  Placement = pos=(-3e-16,0.00920587,-0.105224) rot=(0.043578,0.043578,-0.998099;1.5727rad)
  expr: Constraints[87] = <<params>>.switch_width / 2
  expr: Constraints[88] = <<params>>.switch_width / 2
  sketch-geometry (31):
    g0: LineSegment StartX=-21.3452 StartY=10.975 StartZ=0 EndX=-21.3452 EndY=7.975 EndZ=0
    g1: LineSegment StartX=-21.3452 StartY=7.975 StartZ=0 EndX=-22.5452 EndY=7.975 EndZ=0
    g2: LineSegment StartX=-22.5452 StartY=7.975 StartZ=0 EndX=-22.5452 EndY=6.15 EndZ=0
    g3: LineSegment StartX=-22.5452 StartY=6.15 StartZ=0 EndX=-28.8152 EndY=6.15 EndZ=0
    g4: LineSegment StartX=-28.8152 StartY=6.15 StartZ=0 EndX=-28.8152 EndY=5.275 EndZ=0
    g5: LineSegment StartX=-28.8152 StartY=5.275 StartZ=0 EndX=-31.6152 EndY=5.275 EndZ=0
    g6: LineSegment StartX=-31.6152 StartY=5.275 StartZ=0 EndX=-31.6152 EndY=6.15 EndZ=0
    g7: LineSegment StartX=-31.6152 StartY=6.15 StartZ=0 EndX=-34.8452 EndY=6.15 EndZ=0
    g8: LineSegment StartX=-34.8452 StartY=6.15 StartZ=0 EndX=-34.8452 EndY=12.8 EndZ=0
    g9: LineSegment StartX=-34.8452 StartY=12.8 StartZ=0 EndX=-34.0452 EndY=12.8 EndZ=0
    g10: LineSegment StartX=-34.0452 StartY=12.8 StartZ=0 EndX=-34.0452 EndY=29.95 EndZ=0
    g11: LineSegment StartX=-34.0452 StartY=29.95 StartZ=0 EndX=-34.8452 EndY=29.95 EndZ=0
    g12: LineSegment StartX=-34.8452 StartY=29.95 StartZ=0 EndX=-34.8452 EndY=36.6 EndZ=0
    g13: LineSegment StartX=-34.8452 StartY=36.6 StartZ=0 EndX=-31.6152 EndY=36.6 EndZ=0
    g14: LineSegment StartX=-31.6152 StartY=36.6 StartZ=0 EndX=-31.6152 EndY=37.475 EndZ=0
    g15: LineSegment StartX=-31.6152 StartY=37.475 StartZ=0 EndX=-28.8152 EndY=37.475 EndZ=0
    g16: LineSegment StartX=-28.8152 StartY=37.475 StartZ=0 EndX=-28.8152 EndY=36.6 EndZ=0
    g17: LineSegment StartX=-28.8152 StartY=36.6 StartZ=0 EndX=-22.5452 EndY=36.6 EndZ=0
    g18: LineSegment StartX=-22.5452 StartY=36.6 StartZ=0 EndX=-22.5452 EndY=34.775 EndZ=0
    g19: LineSegment StartX=-22.5452 StartY=34.775 StartZ=0 EndX=-21.3452 EndY=34.775 EndZ=0
    g20: LineSegment StartX=-21.3452 StartY=34.775 StartZ=0 EndX=-21.3452 EndY=31.775 EndZ=0
    g21: LineSegment StartX=-21.3452 StartY=31.775 StartZ=0 EndX=-22.5452 EndY=31.775 EndZ=0
    g22: LineSegment StartX=-22.5452 StartY=31.775 StartZ=0 EndX=-22.5452 EndY=29.95 EndZ=0
    g23: LineSegment StartX=-22.5452 StartY=29.95 StartZ=0 EndX=-23.3452 EndY=29.95 EndZ=0
    g24: LineSegment StartX=-23.3452 StartY=29.95 StartZ=0 EndX=-23.3452 EndY=12.8 EndZ=0
    g25: LineSegment StartX=-23.3452 StartY=12.8 StartZ=0 EndX=-22.5452 EndY=12.8 EndZ=0
    g26: LineSegment StartX=-22.5452 StartY=12.8 StartZ=0 EndX=-22.5452 EndY=10.975 EndZ=0
    g27: LineSegment StartX=-22.5452 StartY=10.975 StartZ=0 EndX=-21.3452 EndY=10.975 EndZ=0
    g28: LineSegment [constr] StartX=-23.3452 StartY=21.375 StartZ=0 EndX=-34.0452 EndY=21.375 EndZ=0
    g29: LineSegment [constr] StartX=-29.3152 StartY=5.275 StartZ=0 EndX=-29.3152 EndY=37.475 EndZ=0
    g30: LineSegment [constr] StartX=-21.3452 StartY=9.475 StartZ=0 EndX=-34.8452 EndY=9.475 EndZ=0
  constraints (90):
    c: Vertical(g0)
    c: Coincident(g0,g1)
    c: Horizontal(g1)
    c: Coincident(g1,g2)
    c: Vertical(g2)
    c: Coincident(g2,g3)
    c: Horizontal(g3)
    c: Coincident(g3,g4)
    c: Vertical(g4)
    c: Coincident(g4,g5)
    c: Coincident(g5,g6)
    c: Coincident(g6,g7)
    c: Horizontal(g7)
    c: Coincident(g7,g8)
    c: Vertical(g8)
    c: Coincident(g8,g9)
    c: Coincident(g9,g10)
    c: Vertical(g10)
    c: Coincident(g10,g11)
    c: Horizontal(g11)
    c: Coincident(g11,g12)
    c: Vertical(g12)
    c: Coincident(g12,g13)
    c: Coincident(g13,g14)
    c: Vertical(g14)
    c: Coincident(g14,g15)
    c: Horizontal(g15)
    c: Coincident(g15,g16)
    c: Coincident(g16,g17)
    c: Horizontal(g17)
    c: Coincident(g17,g18)
    c: Coincident(g18,g19)
    c: Horizontal(g19)
    c: Coincident(g19,g20)
    c: Vertical(g20)
    c: Coincident(g20,g21)
    c: Coincident(g21,g22)
    c: Coincident(g22,g23)
    c: Coincident(g23,g24)
    c: Vertical(g24)
    c: Coincident(g24,g25)
    c: Coincident(g25,g26)
    c: Vertical(g26)
    c: Coincident(g26,g27)
    c: Coincident(g27,g0)
    c: Horizontal(g27)
    c: Horizontal(g25)
    c: Horizontal(g9)
    c: Vertical(g6)
    c: Horizontal(g5)
    c: Horizontal(g13)
    c: Vertical(g18)
    c: Horizontal(g21)
    c: Vertical(g22)
    c: Horizontal(g23)
    c: Symmetric(g24,g24,g28)
    c: PointOnObject(g28,g10)
    c: Horizontal(g28)
    c: PointOnObject(g29,g5)
    c: PointOnObject(g29,g15)
    c: Vertical(g29)
    c: Vertical(g16)
    c: Symmetric(g11,g8,g28)
    c: Symmetric(g14,g5,g28)
    c: Symmetric(g0,g19,g28)
    c: Symmetric(g21,g26,g28)
    c: Equal(g15,g5)
    c: Equal(g8,g12)
    c: Symmetric(g0,g0,g30)
    c: Horizontal(g30)
    c: Distance(g29,g4) = 0.5
    c: Distance(g23,g25) = 17.15
    c: Distance(g21,g27) = 20.8
    c: Distance(g19,g1) = 26.8
    c: Distance(g13,g7) = 30.45
    c: Distance(g15,g5) = 32.2
    c: PointOnObject(g6,g3)
    c: PointOnObject(g24,g9)
    c: Distance(g2,g29) = 6.77
    c: Distance(g29,g0) = 7.97
    c: PointOnObject(g26,g2)
    c: PointOnObject(g13,g17)
    c: PointOnObject(g18,g22)
    c: Distance(g12,g29) = 5.53
    c: Distance(g14,g29) = 2.3
    c: Distance(g24,g29) = 5.97
    c: Distance(g10,g29) = 4.73
    c: Distance(g-3,g28) = 7
    c: Distance(g-3,g29) = 7
    c: PointOnObject(g30,g8)
FEATURE [PartDesign::Pocket] Pocket012
  BaseFeature = -> LinearPattern011
  Direction = (-3.3e-15,0.0871557,-0.996195)
  Length = 0
  Length2 = 5
  Placement = pos=(0,0,0) rot=(0.57735,0.57735,0.57735;2.0944rad)
  Profile = -> Sketch013
  ReferenceAxis = -> Sketch013 [N_Axis]
  Refine = true
  Suppressed = false
  Type = 3
  UpToFace = -> LinearPattern011 [Face71]
FEATURE [Sketcher::SketchObject] Sketch014
  ArcFitTolerance = 1e-06
  AttachmentSupport = -> [Pocket012]
  ExternalGeometry = -> [LinearPattern011,Pocket012]
  FullyConstrained = true
  MakeInternals = false
  MapMode = 5
  Placement = pos=(-1.37e-14,0.609502,-3.45666) rot=(0.086827,0.086827,-0.992433;1.57839rad)
  expr: Constraints[70] = Sketch013.Constraints[70]
  expr: Constraints[71] = Sketch013.Constraints[71]
  expr: Constraints[72] = Sketch013.Constraints[72]
  expr: Constraints[73] = Sketch013.Constraints[73]
  expr: Constraints[74] = Sketch013.Constraints[74]
  expr: Constraints[75] = Sketch013.Constraints[75]
  expr: Constraints[78] = Sketch013.Constraints[78]
  expr: Constraints[79] = Sketch013.Constraints[79]
  expr: Constraints[83] = Sketch013.Constraints[83]
  expr: Constraints[84] = Sketch013.Constraints[84]
  expr: Constraints[85] = Sketch013.Constraints[85]
  expr: Constraints[86] = Sketch013.Constraints[86]
  expr: Constraints[88] = <<params>>.switch_width / 2
  expr: Constraints[89] = <<params>>.switch_width / 2
  sketch-geometry (31):
    g0: LineSegment StartX=-40.6874 StartY=253.225 StartZ=0 EndX=-40.6874 EndY=250.225 EndZ=0
    g1: LineSegment StartX=-40.6874 StartY=250.225 StartZ=0 EndX=-41.8874 EndY=250.225 EndZ=0
    g2: LineSegment StartX=-41.8874 StartY=250.225 StartZ=0 EndX=-41.8874 EndY=248.4 EndZ=0
    g3: LineSegment StartX=-41.8874 StartY=248.4 StartZ=0 EndX=-48.1574 EndY=248.4 EndZ=0
    g4: LineSegment StartX=-48.1574 StartY=248.4 StartZ=0 EndX=-48.1574 EndY=247.525 EndZ=0
    g5: LineSegment StartX=-48.1574 StartY=247.525 StartZ=0 EndX=-50.9574 EndY=247.525 EndZ=0
    g6: LineSegment StartX=-50.9574 StartY=247.525 StartZ=0 EndX=-50.9574 EndY=248.4 EndZ=0
    g7: LineSegment StartX=-50.9574 StartY=248.4 StartZ=0 EndX=-54.1874 EndY=248.4 EndZ=0
    g8: LineSegment StartX=-54.1874 StartY=248.4 StartZ=0 EndX=-54.1874 EndY=255.05 EndZ=0
    g9: LineSegment StartX=-54.1874 StartY=255.05 StartZ=0 EndX=-53.3874 EndY=255.05 EndZ=0
    g10: LineSegment StartX=-53.3874 StartY=255.05 StartZ=0 EndX=-53.3874 EndY=272.2 EndZ=0
    g11: LineSegment StartX=-53.3874 StartY=272.2 StartZ=0 EndX=-54.1874 EndY=272.2 EndZ=0
    g12: LineSegment StartX=-54.1874 StartY=272.2 StartZ=0 EndX=-54.1874 EndY=278.85 EndZ=0
    g13: LineSegment StartX=-54.1874 StartY=278.85 StartZ=0 EndX=-50.9574 EndY=278.85 EndZ=0
    g14: LineSegment StartX=-50.9574 StartY=278.85 StartZ=0 EndX=-50.9574 EndY=279.725 EndZ=0
    g15: LineSegment StartX=-50.9574 StartY=279.725 StartZ=0 EndX=-48.1574 EndY=279.725 EndZ=0
    g16: LineSegment StartX=-48.1574 StartY=279.725 StartZ=0 EndX=-48.1574 EndY=278.85 EndZ=0
    g17: LineSegment StartX=-48.1574 StartY=278.85 StartZ=0 EndX=-41.8874 EndY=278.85 EndZ=0
    g18: LineSegment StartX=-41.8874 StartY=278.85 StartZ=0 EndX=-41.8874 EndY=277.025 EndZ=0
    g19: LineSegment StartX=-41.8874 StartY=277.025 StartZ=0 EndX=-40.6874 EndY=277.025 EndZ=0
    g20: LineSegment StartX=-40.6874 StartY=277.025 StartZ=0 EndX=-40.6874 EndY=274.025 EndZ=0
    g21: LineSegment StartX=-40.6874 StartY=274.025 StartZ=0 EndX=-41.8874 EndY=274.025 EndZ=0
    g22: LineSegment StartX=-41.8874 StartY=274.025 StartZ=0 EndX=-41.8874 EndY=272.2 EndZ=0
    g23: LineSegment StartX=-41.8874 StartY=272.2 StartZ=0 EndX=-42.6874 EndY=272.2 EndZ=0
    g24: LineSegment StartX=-42.6874 StartY=272.2 StartZ=0 EndX=-42.6874 EndY=255.05 EndZ=0
    g25: LineSegment StartX=-42.6874 StartY=255.05 StartZ=0 EndX=-41.8874 EndY=255.05 EndZ=0
    g26: LineSegment StartX=-41.8874 StartY=255.05 StartZ=0 EndX=-41.8874 EndY=253.225 EndZ=0
    g27: LineSegment StartX=-41.8874 StartY=253.225 StartZ=0 EndX=-40.6874 EndY=253.225 EndZ=0
    g28: LineSegment [constr] StartX=-42.6874 StartY=263.625 StartZ=0 EndX=-53.3874 EndY=263.625 EndZ=0
    g29: LineSegment [constr] StartX=-48.6574 StartY=247.525 StartZ=0 EndX=-48.6574 EndY=279.725 EndZ=0
    g30: LineSegment [constr] StartX=-40.6874 StartY=251.725 StartZ=0 EndX=-54.1874 EndY=251.725 EndZ=0
  constraints (90):
    c: Vertical(g0)
    c: Coincident(g0,g1)
    c: Horizontal(g1)
    c: Coincident(g1,g2)
    c: Vertical(g2)
    c: Coincident(g2,g3)
    c: Horizontal(g3)
    c: Coincident(g3,g4)
    c: Vertical(g4)
    c: Coincident(g4,g5)
    c: Coincident(g5,g6)
    c: Coincident(g6,g7)
    c: Horizontal(g7)
    c: Coincident(g7,g8)
    c: Vertical(g8)
    c: Coincident(g8,g9)
    c: Coincident(g9,g10)
    c: Vertical(g10)
    c: Coincident(g10,g11)
    c: Horizontal(g11)
    c: Coincident(g11,g12)
    c: Vertical(g12)
    c: Coincident(g12,g13)
    c: Coincident(g13,g14)
    c: Vertical(g14)
    c: Coincident(g14,g15)
    c: Horizontal(g15)
    c: Coincident(g15,g16)
    c: Coincident(g16,g17)
    c: Horizontal(g17)
    c: Coincident(g17,g18)
    c: Coincident(g18,g19)
    c: Horizontal(g19)
    c: Coincident(g19,g20)
    c: Vertical(g20)
    c: Coincident(g20,g21)
    c: Coincident(g21,g22)
    c: Coincident(g22,g23)
    c: Coincident(g23,g24)
    c: Vertical(g24)
    c: Coincident(g24,g25)
    c: Coincident(g25,g26)
    c: Vertical(g26)
    c: Coincident(g26,g27)
    c: Coincident(g27,g0)
    c: Horizontal(g27)
    c: Horizontal(g25)
    c: Horizontal(g9)
    c: Vertical(g6)
    c: Horizontal(g5)
    c: Horizontal(g13)
    c: Vertical(g18)
    c: Horizontal(g21)
    c: Vertical(g22)
    c: Horizontal(g23)
    c: Symmetric(g24,g24,g28)
    c: PointOnObject(g28,g10)
    c: Horizontal(g28)
    c: PointOnObject(g29,g5)
    c: PointOnObject(g29,g15)
    c: Vertical(g29)
    c: Vertical(g16)
    c: Symmetric(g11,g8,g28)
    c: Symmetric(g14,g5,g28)
    c: Symmetric(g0,g19,g28)
    c: Symmetric(g21,g26,g28)
    c: Equal(g15,g5)
    c: Equal(g8,g12)
    c: Symmetric(g0,g0,g30)
    c: Horizontal(g30)
    c: Distance(g29,g4) = 0.5
    c: Distance(g23,g25) = 17.15
    c: Distance(g21,g27) = 20.8
    c: Distance(g19,g1) = 26.8
    c: Distance(g13,g7) = 30.45
    c: Distance(g15,g5) = 32.2
    c: PointOnObject(g6,g3)
    c: PointOnObject(g24,g9)
    c: Distance(g2,g29) = 6.77
    c: Distance(g29,g0) = 7.97
    c: PointOnObject(g26,g2)
    c: PointOnObject(g13,g17)
    c: PointOnObject(g18,g22)
    c: Distance(g12,g29) = 5.53
    c: Distance(g14,g29) = 2.3
    c: Distance(g24,g29) = 5.97
    c: Distance(g10,g29) = 4.73
    c: PointOnObject(g30,g8)
    c: Distance(g-4,g28) = 7
    c: Distance(g-4,g29) = 7
FEATURE [Sketcher::SketchObject] Sketch015
  ArcFitTolerance = 1e-06
  AttachmentSupport = -> [Pocket012]
  ExternalGeometry = -> [LinearPattern011,Pocket012]
  FullyConstrained = true
  MakeInternals = false
  MapMode = 5
  Placement = pos=(-7.02e-14,5.23241,-14.3759) rot=(0.171088,0.171088,-0.970288;1.60095rad)
  expr: Constraints[70] = Sketch013.Constraints[70]
  expr: Constraints[71] = Sketch013.Constraints[71]
  expr: Constraints[72] = Sketch013.Constraints[72]
  expr: Constraints[73] = Sketch013.Constraints[73]
  expr: Constraints[74] = Sketch013.Constraints[74]
  expr: Constraints[75] = Sketch013.Constraints[75]
  expr: Constraints[78] = Sketch013.Constraints[78]
  expr: Constraints[79] = Sketch013.Constraints[79]
  expr: Constraints[83] = Sketch013.Constraints[83]
  expr: Constraints[84] = Sketch013.Constraints[84]
  expr: Constraints[85] = Sketch013.Constraints[85]
  expr: Constraints[86] = Sketch013.Constraints[86]
  expr: Constraints[88] = <<params>>.switch_width / 2
  expr: Constraints[89] = <<params>>.switch_width / 2
  sketch-geometry (31):
    g0: LineSegment StartX=-78.1163 StartY=255.6 StartZ=0 EndX=-78.1163 EndY=252.6 EndZ=0
    g1: LineSegment StartX=-78.1163 StartY=252.6 StartZ=0 EndX=-79.3163 EndY=252.6 EndZ=0
    g2: LineSegment StartX=-79.3163 StartY=252.6 StartZ=0 EndX=-79.3163 EndY=250.775 EndZ=0
    g3: LineSegment StartX=-79.3163 StartY=250.775 StartZ=0 EndX=-85.5863 EndY=250.775 EndZ=0
    g4: LineSegment StartX=-85.5863 StartY=250.775 StartZ=0 EndX=-85.5863 EndY=249.9 EndZ=0
    g5: LineSegment StartX=-85.5863 StartY=249.9 StartZ=0 EndX=-88.3863 EndY=249.9 EndZ=0
    g6: LineSegment StartX=-88.3863 StartY=249.9 StartZ=0 EndX=-88.3863 EndY=250.775 EndZ=0
    g7: LineSegment StartX=-88.3863 StartY=250.775 StartZ=0 EndX=-91.6163 EndY=250.775 EndZ=0
    g8: LineSegment StartX=-91.6163 StartY=250.775 StartZ=0 EndX=-91.6163 EndY=257.425 EndZ=0
    g9: LineSegment StartX=-91.6163 StartY=257.425 StartZ=0 EndX=-90.8163 EndY=257.425 EndZ=0
    g10: LineSegment StartX=-90.8163 StartY=257.425 StartZ=0 EndX=-90.8163 EndY=274.575 EndZ=0
    g11: LineSegment StartX=-90.8163 StartY=274.575 StartZ=0 EndX=-91.6163 EndY=274.575 EndZ=0
    g12: LineSegment StartX=-91.6163 StartY=274.575 StartZ=0 EndX=-91.6163 EndY=281.225 EndZ=0
    g13: LineSegment StartX=-91.6163 StartY=281.225 StartZ=0 EndX=-88.3863 EndY=281.225 EndZ=0
    g14: LineSegment StartX=-88.3863 StartY=281.225 StartZ=0 EndX=-88.3863 EndY=282.1 EndZ=0
    g15: LineSegment StartX=-88.3863 StartY=282.1 StartZ=0 EndX=-85.5863 EndY=282.1 EndZ=0
    g16: LineSegment StartX=-85.5863 StartY=282.1 StartZ=0 EndX=-85.5863 EndY=281.225 EndZ=0
    g17: LineSegment StartX=-85.5863 StartY=281.225 StartZ=0 EndX=-79.3163 EndY=281.225 EndZ=0
    g18: LineSegment StartX=-79.3163 StartY=281.225 StartZ=0 EndX=-79.3163 EndY=279.4 EndZ=0
    g19: LineSegment StartX=-79.3163 StartY=279.4 StartZ=0 EndX=-78.1163 EndY=279.4 EndZ=0
    g20: LineSegment StartX=-78.1163 StartY=279.4 StartZ=0 EndX=-78.1163 EndY=276.4 EndZ=0
    g21: LineSegment StartX=-78.1163 StartY=276.4 StartZ=0 EndX=-79.3163 EndY=276.4 EndZ=0
    g22: LineSegment StartX=-79.3163 StartY=276.4 StartZ=0 EndX=-79.3163 EndY=274.575 EndZ=0
    g23: LineSegment StartX=-79.3163 StartY=274.575 StartZ=0 EndX=-80.1163 EndY=274.575 EndZ=0
    g24: LineSegment StartX=-80.1163 StartY=274.575 StartZ=0 EndX=-80.1163 EndY=257.425 EndZ=0
    g25: LineSegment StartX=-80.1163 StartY=257.425 StartZ=0 EndX=-79.3163 EndY=257.425 EndZ=0
    g26: LineSegment StartX=-79.3163 StartY=257.425 StartZ=0 EndX=-79.3163 EndY=255.6 EndZ=0
    g27: LineSegment StartX=-79.3163 StartY=255.6 StartZ=0 EndX=-78.1163 EndY=255.6 EndZ=0
    g28: LineSegment [constr] StartX=-80.1163 StartY=266 StartZ=0 EndX=-90.8163 EndY=266 EndZ=0
    g29: LineSegment [constr] StartX=-86.0863 StartY=249.9 StartZ=0 EndX=-86.0863 EndY=282.1 EndZ=0
    g30: LineSegment [constr] StartX=-78.1163 StartY=254.1 StartZ=0 EndX=-91.6163 EndY=254.1 EndZ=0
  constraints (90):
    c: Vertical(g0)
    c: Coincident(g0,g1)
    c: Horizontal(g1)
    c: Coincident(g1,g2)
    c: Vertical(g2)
    c: Coincident(g2,g3)
    c: Horizontal(g3)
    c: Coincident(g3,g4)
    c: Vertical(g4)
    c: Coincident(g4,g5)
    c: Coincident(g5,g6)
    c: Coincident(g6,g7)
    c: Horizontal(g7)
    c: Coincident(g7,g8)
    c: Vertical(g8)
    c: Coincident(g8,g9)
    c: Coincident(g9,g10)
    c: Vertical(g10)
    c: Coincident(g10,g11)
    c: Horizontal(g11)
    c: Coincident(g11,g12)
    c: Vertical(g12)
    c: Coincident(g12,g13)
    c: Coincident(g13,g14)
    c: Vertical(g14)
    c: Coincident(g14,g15)
    c: Horizontal(g15)
    c: Coincident(g15,g16)
    c: Coincident(g16,g17)
    c: Horizontal(g17)
    c: Coincident(g17,g18)
    c: Coincident(g18,g19)
    c: Horizontal(g19)
    c: Coincident(g19,g20)
    c: Vertical(g20)
    c: Coincident(g20,g21)
    c: Coincident(g21,g22)
    c: Coincident(g22,g23)
    c: Coincident(g23,g24)
    c: Vertical(g24)
    c: Coincident(g24,g25)
    c: Coincident(g25,g26)
    c: Vertical(g26)
    c: Coincident(g26,g27)
    c: Coincident(g27,g0)
    c: Horizontal(g27)
    c: Horizontal(g25)
    c: Horizontal(g9)
    c: Vertical(g6)
    c: Horizontal(g5)
    c: Horizontal(g13)
    c: Vertical(g18)
    c: Horizontal(g21)
    c: Vertical(g22)
    c: Horizontal(g23)
    c: Symmetric(g24,g24,g28)
    c: PointOnObject(g28,g10)
    c: Horizontal(g28)
    c: PointOnObject(g29,g5)
    c: PointOnObject(g29,g15)
    c: Vertical(g29)
    c: Vertical(g16)
    c: Symmetric(g11,g8,g28)
    c: Symmetric(g14,g5,g28)
    c: Symmetric(g0,g19,g28)
    c: Symmetric(g21,g26,g28)
    c: Equal(g15,g5)
    c: Equal(g8,g12)
    c: Symmetric(g0,g0,g30)
    c: Horizontal(g30)
    c: Distance(g29,g4) = 0.5
    c: Distance(g23,g25) = 17.15
    c: Distance(g21,g27) = 20.8
    c: Distance(g19,g1) = 26.8
    c: Distance(g13,g7) = 30.45
    c: Distance(g15,g5) = 32.2
    c: PointOnObject(g6,g3)
    c: PointOnObject(g24,g9)
    c: Distance(g2,g29) = 6.77
    c: Distance(g29,g0) = 7.97
    c: PointOnObject(g26,g2)
    c: PointOnObject(g13,g17)
    c: PointOnObject(g18,g22)
    c: Distance(g12,g29) = 5.53
    c: Distance(g14,g29) = 2.3
    c: Distance(g24,g29) = 5.97
    c: Distance(g10,g29) = 4.73
    c: PointOnObject(g30,g8)
    c: Distance(g-4,g28) = 7
    c: Distance(g-4,g29) = 7
FEATURE [PartDesign::Pocket] Pocket013
  BaseFeature = -> Pocket012
  Direction = (-3.9e-15,0.173648,-0.984808)
  Length = 0
  Length2 = 5
  Placement = pos=(0,0,0) rot=(0.57735,0.57735,0.57735;2.0944rad)
  Profile = -> Sketch014
  ReferenceAxis = -> Sketch014 [N_Axis]
  Refine = true
  Suppressed = false
  Type = 3
  UpToFace = -> Pocket012 [Face73]
FEATURE [PartDesign::Pocket] Pocket014
  BaseFeature = -> Pocket013
  Direction = (-4.6e-15,0.34202,-0.939693)
  Length = 0
  Length2 = 5
  Placement = pos=(0,0,0) rot=(0.57735,0.57735,0.57735;2.0944rad)
  Profile = -> Sketch015
  ReferenceAxis = -> Sketch015 [N_Axis]
  Refine = true
  Suppressed = false
  Type = 3
  UpToFace = -> Pocket013 [Face77]
FEATURE [PartDesign::LinearPattern] LinearPattern012
  BaseFeature = -> Pocket014
  Direction = -> X_Axis002
  Length = 237.5
  Mode = 0
  Occurrences = 2
  Offset = 237.5
  Originals = -> [Pocket012]
  Placement = pos=(0,0,0) rot=(0.57735,0.57735,0.57735;2.0944rad)
  Refine = true
  Suppressed = false
  TransformMode = 0
  expr: Length = <<params>>.spacing_x * (<<params>>.column_count - (<<params>>.enterKey_width + <<params>>.shiftKey_width) / 2)
FEATURE [PartDesign::Body] Body
  AllowCompound = false
  Group = -> [Sketch,Pad,Sketch001,Sketch002,Sketch003,Sketch004,Sketch005,Sketch006,Pocket,Pocket001,Pocket002,Pocket003,Pocket004,Pocket005,LinearPattern,LinearPattern001,LinearPattern002,LinearPattern003,LinearPattern004,LinearPattern005,LinearPattern006,LinearPattern007,LinearPattern008,LinearPattern009,Sketch007,Sketch008,Sketch009,Sketch010,Sketch011,Sketch012,LinearPattern010,Pocket006,Pocket007,+12 more]
  Origin = -> Origin002
  Tip = -> LinearPattern012
FEATURE [App::Part] Part  label="Plate"
  Group = -> [Body]
  Material = -> Spreadsheet
  Origin = -> Origin001
FEATURE [App::FeaturePython] GroundedJoint  # Assembly grounded joint (typed FeaturePython)
  ObjectToGround = -> Part
FEATURE [Assembly::JointGroup] Joints
  Group = -> [GroundedJoint]
FEATURE [App::Part] Part001  label="Case_Left"
  Origin = -> Origin003
FEATURE [Assembly::AssemblyObject] Assembly  label="Main_Section"
  Group = -> [Joints,Part,Part001,Spreadsheet,GroundedJoint]
  Origin = -> Origin
  Type = Assembly
